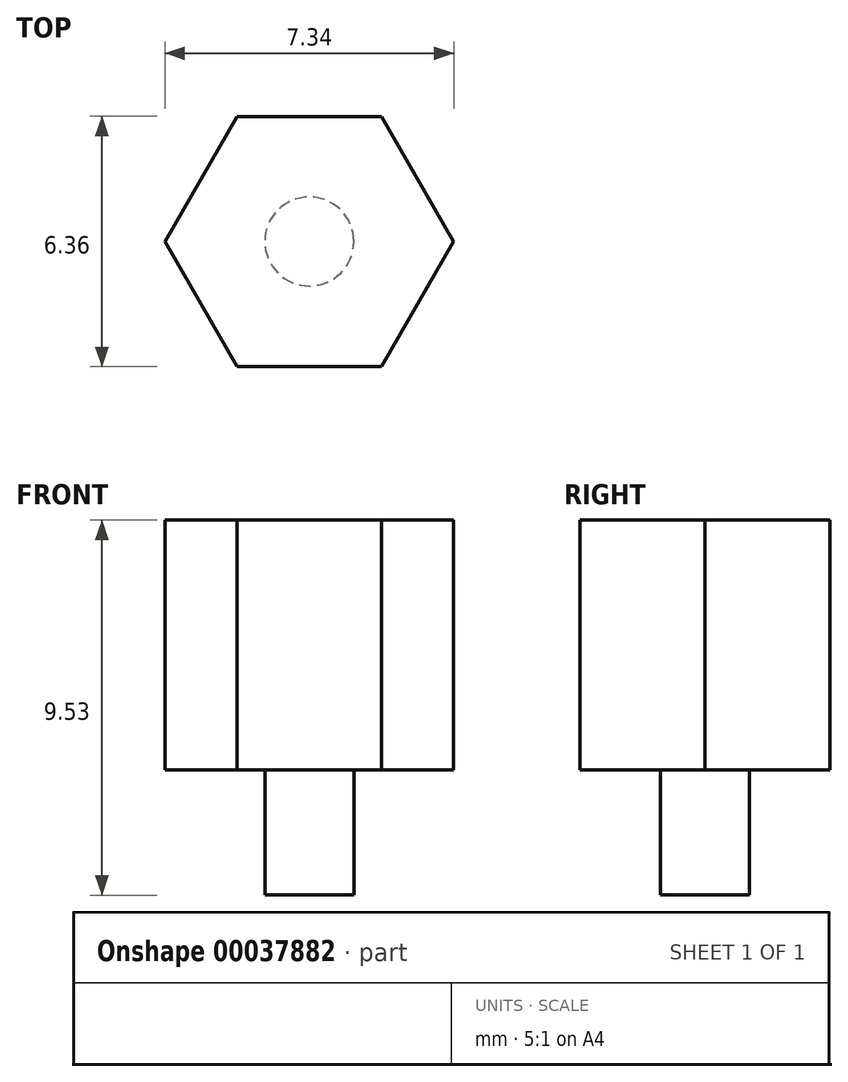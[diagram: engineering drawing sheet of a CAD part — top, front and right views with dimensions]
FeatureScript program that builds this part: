
annotation { "Feature Type Name" : "Feature", "Feature Type Description" : "" }
export const myFeature = defineFeature(function(context is Context, id is Id, definition is map)
    precondition{}
    {
        {
            var Q0;
            Q0=qCreatedBy(makeId("Top.planeOp"),FACE);
            var sketch = newSketch(context, id + "F0", { "sketchPlane" : qUnion([Q0])});
            skCircle(sketch, "E0.cCircle", {"center": v(0, 0) * mm, "radius": 3.18 * mm, "construction": true});
            skLineSegment(sketch, "E0.0", {"start": v(1.83, -3.18) * mm, "end": v(-1.83, -3.18) * mm});
            skLineSegment(sketch, "E0.1", {"start": v(-1.83, -3.18) * mm, "end": v(-3.67, 0) * mm});
            skLineSegment(sketch, "E0.2", {"start": v(-3.67, 0) * mm, "end": v(-1.83, 3.18) * mm});
            skLineSegment(sketch, "E0.3", {"start": v(-1.83, 3.17) * mm, "end": v(1.83, 3.18) * mm});
            skLineSegment(sketch, "E0.4", {"start": v(1.83, 3.18) * mm, "end": v(3.67, 0) * mm});
            skLineSegment(sketch, "E0.5", {"start": v(3.67, 0) * mm, "end": v(1.83, -3.17) * mm});
            skPoint(sketch, "E0.0.midPoint", {"position": v(0, -3.18) * mm});
            skSolve(sketch);
        }
        {
            var Q0;
            Q0 = qSketchRegion(id + "F0", true);
            extrude(context, id + "F1", {"entities" : qUnion([Q0]), "depth" : 6.35 * mm});
        }
        {
            var Q0;
            Q0=makeQuery(id+"F1.opExtrude","CAP_FACE",FACE,{"disambiguationData":[OSD([sQuery(id+"F0.wireOp",EDGE,"E0.0"),sQuery(id+"F0.wireOp",EDGE,"E0.1"),sQuery(id+"F0.wireOp",EDGE,"E0.2"),sQuery(id+"F0.wireOp",EDGE,"E0.3"),sQuery(id+"F0.wireOp",EDGE,"E0.4"),sQuery(id+"F0.wireOp",EDGE,"E0.5")])],"isStart":true});
            var sketch = newSketch(context, id + "F2", { "sketchPlane" : qUnion([Q0])});
            skCircle(sketch, "E1", {"center": v(0, 0) * mm, "radius": 1.13 * mm});
            skSolve(sketch);
        }
        {
            var Q0;
            Q0 = qSketchRegion(id + "F2", true);
            extrude(context, id + "F3", {"entities" : qUnion([Q0]), "operationType" : NewBodyOperationType.ADD, "depth" : 3.17 * mm});
        }
    });
